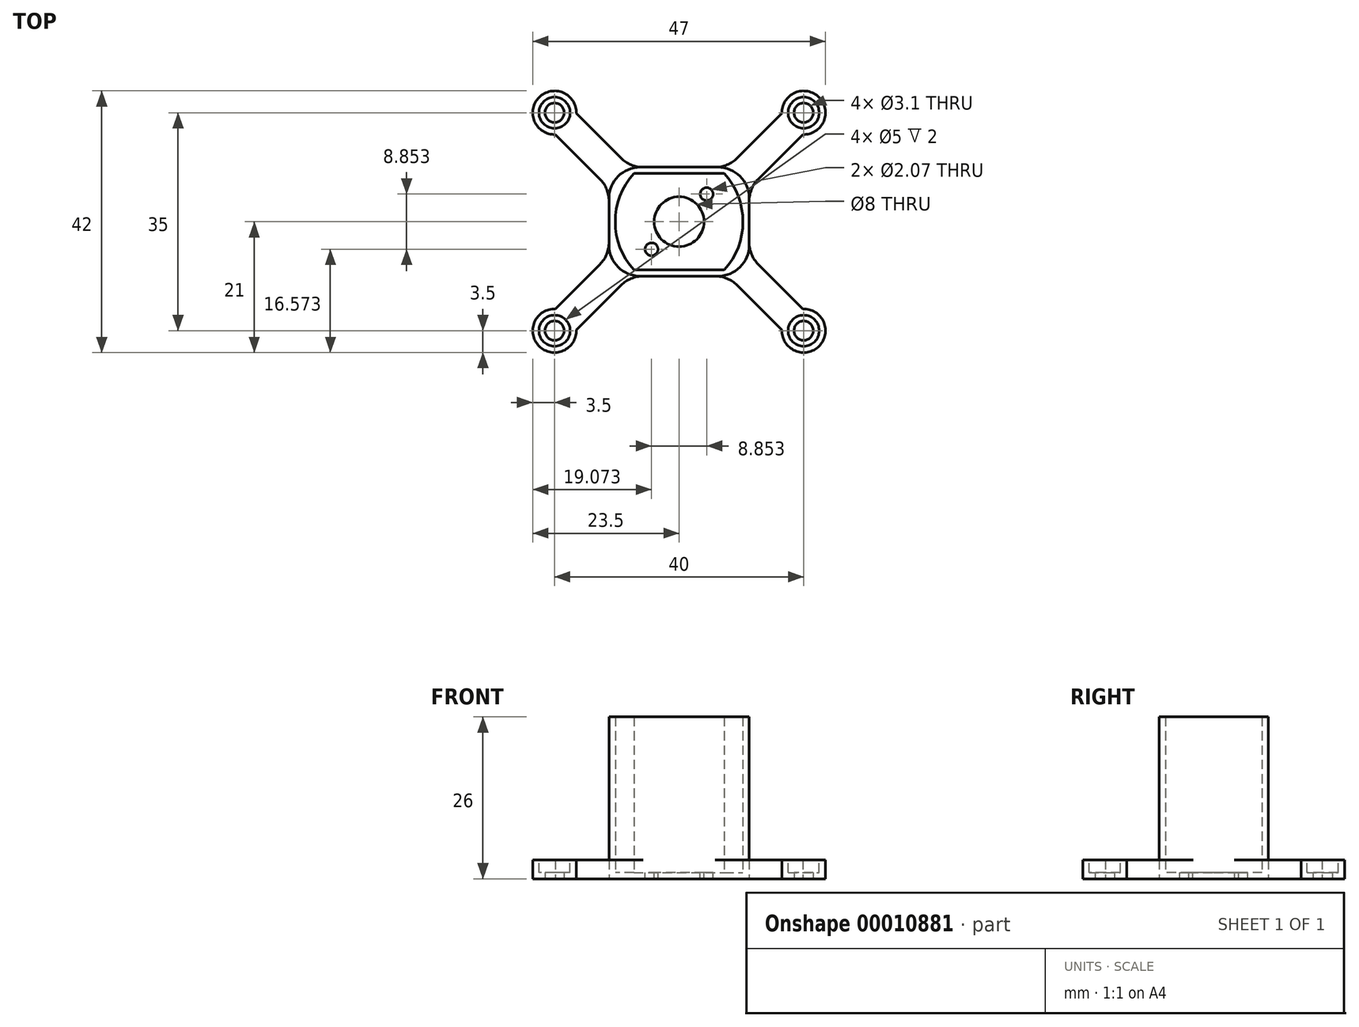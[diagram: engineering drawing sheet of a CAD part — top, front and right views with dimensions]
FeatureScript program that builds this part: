
annotation { "Feature Type Name" : "Feature", "Feature Type Description" : "" }
export const myFeature = defineFeature(function(context is Context, id is Id, definition is map)
    precondition{}
    {
        {
            var Q0;
            Q0=qCreatedBy(makeId("Top.planeOp"),FACE);
            var sketch = newSketch(context, id + "F0", { "sketchPlane" : qUnion([Q0])});
            skLineSegment(sketch, "E0.bottom", {"start": v(-7.25, 7.75) * mm, "end": v(7.25, 7.75) * mm});
            skLineSegment(sketch, "E0.top", {"start": v(-7.25, -7.75) * mm, "end": v(7.25, -7.75) * mm});
            skLineSegment(sketch, "E0.left", {"start": v(-7.25, 7.75) * mm, "end": v(-7.25, -7.75) * mm, "construction": true});
            skLineSegment(sketch, "E0.right", {"start": v(7.25, 7.75) * mm, "end": v(7.25, -7.75) * mm, "construction": true});
            skArc(sketch, "E1", {"start": v(-7.25, 7.75) * mm, "mid": v(-10.25, 0) * mm, "end": v(-7.25, -7.75) * mm});
            skArc(sketch, "E2", {"start": v(7.25, -7.75) * mm, "mid": v(10.25, 0) * mm, "end": v(7.25, 7.75) * mm});
            skLineSegment(sketch, "E3", {"start": v(-7.25, 7.75) * mm, "end": v(-10.25, 7.75) * mm, "construction": true});
            skLineSegment(sketch, "E4", {"start": v(-10.25, 7.75) * mm, "end": v(-10.25, -7.75) * mm, "construction": true});
            skLineSegment(sketch, "E5", {"start": v(-10.25, -7.75) * mm, "end": v(-7.25, -7.75) * mm, "construction": true});
            skLineSegment(sketch, "E6", {"start": v(7.25, -7.75) * mm, "end": v(10.25, -7.75) * mm, "construction": true});
            skLineSegment(sketch, "E7", {"start": v(10.25, -7.75) * mm, "end": v(10.25, 7.75) * mm, "construction": true});
            skLineSegment(sketch, "E8", {"start": v(10.25, 7.75) * mm, "end": v(7.25, 7.75) * mm, "construction": true});
            skLineSegment(sketch, "E9.bottom", {"start": v(-11.25, 8.75) * mm, "end": v(11.25, 8.75) * mm});
            skLineSegment(sketch, "E9.top", {"start": v(-11.25, -8.75) * mm, "end": v(11.25, -8.75) * mm});
            skLineSegment(sketch, "E9.left", {"start": v(-11.25, 8.75) * mm, "end": v(-11.25, -8.75) * mm});
            skLineSegment(sketch, "E9.right", {"start": v(11.25, 8.75) * mm, "end": v(11.25, -8.75) * mm});
            skPoint(sketch, "E10.visualSharp", {"position": v(-11.25, 8.75) * mm});
            skPoint(sketch, "E11.visualSharp", {"position": v(11.25, 8.75) * mm});
            skPoint(sketch, "E12.visualSharp", {"position": v(11.25, -8.75) * mm});
            skPoint(sketch, "E13.visualSharp", {"position": v(-11.25, -8.75) * mm});
            skLineSegment(sketch, "E14", {"start": v(-1.26, 0) * mm, "end": v(1.26, 0) * mm, "construction": true});
            skPoint(sketch, "E15", {"position": v(0, 0) * mm});
            skLineSegment(sketch, "E16", {"start": v(10.25, -7.75) * mm, "end": v(10.25, -8.75) * mm, "construction": true});
            skLineSegment(sketch, "E17", {"start": v(-10.25, 7.75) * mm, "end": v(-10.25, 8.75) * mm, "construction": true});
            skLineSegment(sketch, "E18", {"start": v(-10.25, 7.75) * mm, "end": v(-11.25, 7.75) * mm, "construction": true});
            skLineSegment(sketch, "E19", {"start": v(10.25, -7.75) * mm, "end": v(11.25, -7.75) * mm, "construction": true});
            skSolve(sketch);
        }
        {
            var Q0;
            Q0=qSketchRegion(id+"F0",true);
            extrude(context, id + "F1", {"entities" : qUnion([Q0]), "depth" : 25 * mm});
        }
        {
            var Q0;
            Q0=qCreatedBy(makeId("Top.planeOp"),FACE);
            var sketch = newSketch(context, id + "F2", { "sketchPlane" : qUnion([Q0])});
            skCircle(sketch, "E20", {"center": v(0, 0) * mm, "radius": 4 * mm});
            skLineSegment(sketch, "E21", {"start": v(-4.43, -4.43) * mm, "end": v(4.43, 4.43) * mm, "construction": true});
            skCircle(sketch, "E22", {"center": v(-4.43, -4.43) * mm, "radius": 1.04 * mm});
            skCircle(sketch, "E23", {"center": v(4.43, 4.43) * mm, "radius": 1.04 * mm});
            skLineSegment(sketch, "E24", {"start": v(0, 0) * mm, "end": v(0, -4) * mm, "construction": true});
            skLineSegment(sketch, "E25.bottom", {"start": v(-11.25, -8.75) * mm, "end": v(11.25, -8.75) * mm});
            skLineSegment(sketch, "E25.top", {"start": v(-11.25, 8.75) * mm, "end": v(11.25, 8.75) * mm});
            skLineSegment(sketch, "E25.left", {"start": v(-11.25, -8.75) * mm, "end": v(-11.25, 8.75) * mm});
            skLineSegment(sketch, "E25.right", {"start": v(11.25, -8.75) * mm, "end": v(11.25, 8.75) * mm});
            skSolve(sketch);
        }
        {
            var Q0;
            Q0=qSketchRegion(id+"F2",true);
            extrude(context, id + "F3", {"entities" : qUnion([Q0]), "operationType" : NewBodyOperationType.ADD, "oppositeDirection" : true, "depth" : 1 * mm});
        }
        {
            var Q0;
            Q0=makeQuery(id+"F3.opExtrude","CAP_FACE",FACE,{"disambiguationData":[OSD([sQuery(id+"F2.wireOp",EDGE,"9aef3d48-fcec-49af-8fe0-c07a83de9d9d.bottom"),sQuery(id+"F2.wireOp",EDGE,"9aef3d48-fcec-49af-8fe0-c07a83de9d9d.top"),sQuery(id+"F2.wireOp",EDGE,"9aef3d48-fcec-49af-8fe0-c07a83de9d9d.left"),sQuery(id+"F2.wireOp",EDGE,"9aef3d48-fcec-49af-8fe0-c07a83de9d9d.right"),sQuery(id+"F2.wireOp",EDGE,"60c8d90f-e83d-42f8-a0dd-aa9fc3caf3ca.filletArc"),sQuery(id+"F2.wireOp",EDGE,"e39097f1-45af-4b58-a32d-9713a406a2f0.filletArc"),sQuery(id+"F2.wireOp",EDGE,"80603ea1-f281-4a3c-b745-80a3f8f7ce23.filletArc"),sQuery(id+"F2.wireOp",EDGE,"1a4f9cfa-e126-41bd-9235-e0dfa8cf3aca.filletArc"),sQuery(id+"F2.wireOp",EDGE,"E20"),sQuery(id+"F2.wireOp",EDGE,"E22"),sQuery(id+"F2.wireOp",EDGE,"E23")])],"isStart":false});
            var sketch = newSketch(context, id + "F4", { "sketchPlane" : qUnion([Q0])});
            skCircle(sketch, "E26", {"center": v(0, 0) * mm, "radius": 17.67 * mm, "construction": true});
            skLineSegment(sketch, "E27", {"start": v(-9.34, 10.21) * mm, "end": v(-16.5, 17.38) * mm});
            skLineSegment(sketch, "E28", {"start": v(-12.71, 6.84) * mm, "end": v(-19.88, 14) * mm});
            skLineSegment(sketch, "E29", {"start": v(-11.25, 8.75) * mm, "end": v(-20, 17.5) * mm, "construction": true});
            skCircle(sketch, "E30", {"center": v(-20, 17.5) * mm, "radius": 1.55 * mm});
            skLineSegment(sketch, "E31", {"start": v(-7.87, 8.75) * mm, "end": v(-11.25, 8.75) * mm, "construction": true});
            skLineSegment(sketch, "E32", {"start": v(-11.25, 8.75) * mm, "end": v(-11.25, 5.37) * mm, "construction": true});
            skPoint(sketch, "E33.visualSharp", {"position": v(-7.87, 8.75) * mm});
            skArc(sketch, "E33.filletArc", {"start": v(-9.34, 10.21) * mm, "mid": v(-7.71, 9.13) * mm, "end": v(-5.8, 8.75) * mm});
            skPoint(sketch, "E34.visualSharp", {"position": v(-11.25, 5.37) * mm});
            skArc(sketch, "E34.filletArc", {"start": v(-11.25, 3.3) * mm, "mid": v(-11.63, 5.21) * mm, "end": v(-12.71, 6.84) * mm});
            skLineSegment(sketch, "E35", {"start": v(-11.25, 3.3) * mm, "end": v(-11.25, 8.75) * mm});
            skLineSegment(sketch, "E36", {"start": v(-5.8, 8.75) * mm, "end": v(-11.25, 8.75) * mm});
            skArc(sketch, "E37", {"start": v(-16.5, 17.38) * mm, "mid": v(-22.47, 19.97) * mm, "end": v(-19.88, 14) * mm});
            skSolve(sketch);
        }
        {
            var Q0;
            Q0=qSketchRegion(id+"F4",true);
            extrude(context, id + "F5", {"entities" : qUnion([Q0]), "oppositeDirection" : true, "depth" : 3 * mm});
        }
        {
            var Q0;
            Q0=makeQuery(id+"F5.opExtrude","CAP_FACE",FACE,{"disambiguationData":[OSD([sQuery(id+"F4.wireOp",EDGE,"E27"),sQuery(id+"F4.wireOp",EDGE,"E28"),sQuery(id+"F4.wireOp",EDGE,"E30"),sQuery(id+"F4.wireOp",EDGE,"E33.filletArc"),sQuery(id+"F4.wireOp",EDGE,"E34.filletArc"),sQuery(id+"F4.wireOp",EDGE,"E35"),sQuery(id+"F4.wireOp",EDGE,"E36"),sQuery(id+"F4.wireOp",EDGE,"E37")])],"isStart":false});
            var sketch = newSketch(context, id + "F6", { "sketchPlane" : qUnion([Q0])});
            skCircle(sketch, "E38", {"center": v(-20, -17.5) * mm, "radius": 2.5 * mm});
            skSolve(sketch);
        }
        {
            var Q0;
            Q0 = qSketchRegion(id + "F6", true);
            extrude(context, id + "F7", {"entities" : qUnion([Q0]), "operationType" : NewBodyOperationType.REMOVE, "oppositeDirection" : true, "depth" : 2 * mm});
        }
        {
            var Q0;
            Q0=makeQuery(id+"F5.opExtrude","SWEPT_BODY",BODY,{"disambiguationData":[OSD([sQuery(id+"F4.wireOp",EDGE,"E27"),sQuery(id+"F4.wireOp",EDGE,"E28"),sQuery(id+"F4.wireOp",EDGE,"1cbfcee3-eb8b-4ad0-8d0a-d4f1d73b6d58"),sQuery(id+"F4.wireOp",EDGE,"E30"),sQuery(id+"F4.wireOp",EDGE,"E33.filletArc"),sQuery(id+"F4.wireOp",EDGE,"E34.filletArc"),sQuery(id+"F4.wireOp",EDGE,"E35"),sQuery(id+"F4.wireOp",EDGE,"E36")])]});
            var Q1;
            Q1=qCreatedBy(makeId("Front.planeOp"),FACE);
            mirror(context, id + "F8", {"entities" : qUnion([Q0]), "mirrorPlane" : qUnion([Q1])});
        }
        {
            var Q0;
            Q0=makeQuery(id+"F8.opPattern","COPY",BODY,{"derivedFrom":makeQuery(id+"F5.opExtrude","SWEPT_BODY",BODY,{"disambiguationData":[OSD([sQuery(id+"F4.wireOp",EDGE,"E27"),sQuery(id+"F4.wireOp",EDGE,"E28"),sQuery(id+"F4.wireOp",EDGE,"1cbfcee3-eb8b-4ad0-8d0a-d4f1d73b6d58"),sQuery(id+"F4.wireOp",EDGE,"E30"),sQuery(id+"F4.wireOp",EDGE,"E33.filletArc"),sQuery(id+"F4.wireOp",EDGE,"E34.filletArc"),sQuery(id+"F4.wireOp",EDGE,"E35"),sQuery(id+"F4.wireOp",EDGE,"E36")])]}),"instanceName":"1"});
            var Q1;
            Q1=makeQuery(id+"F5.opExtrude","SWEPT_BODY",BODY,{"disambiguationData":[OSD([sQuery(id+"F4.wireOp",EDGE,"E27"),sQuery(id+"F4.wireOp",EDGE,"E28"),sQuery(id+"F4.wireOp",EDGE,"1cbfcee3-eb8b-4ad0-8d0a-d4f1d73b6d58"),sQuery(id+"F4.wireOp",EDGE,"E30"),sQuery(id+"F4.wireOp",EDGE,"E33.filletArc"),sQuery(id+"F4.wireOp",EDGE,"E34.filletArc"),sQuery(id+"F4.wireOp",EDGE,"E35"),sQuery(id+"F4.wireOp",EDGE,"E36")])]});
            var Q2;
            Q2=qCreatedBy(makeId("Right.planeOp"),FACE);
            mirror(context, id + "F9", {"operationType" : NewBodyOperationType.ADD, "entities" : qUnion([Q0, Q1]), "mirrorPlane" : qUnion([Q2])});
        }
        {
            var Q0;
            Q0=makeQuery(id+"F3.boolean.opBoolean","MERGE",EDGE,{"derivedFrom":[makeQuery(id+"F1.opExtrude","SWEPT_EDGE",EDGE,{"disambiguationData":[OSD([sQuery(id+"F0.wireOp",EDGE,"E9.bottom"),sQuery(id+"F0.wireOp",EDGE,"E9.left")])]}),makeQuery(id+"F3.opExtrude","SWEPT_EDGE",EDGE,{"disambiguationData":[OSD([sQuery(id+"F2.wireOp",EDGE,"E25.top"),sQuery(id+"F2.wireOp",EDGE,"E25.left")])]})]});
            var Q1;
            Q1=makeQuery(id+"F3.boolean.opBoolean","MERGE",EDGE,{"derivedFrom":[makeQuery(id+"F1.opExtrude","SWEPT_EDGE",EDGE,{"disambiguationData":[OSD([sQuery(id+"F0.wireOp",EDGE,"E9.top"),sQuery(id+"F0.wireOp",EDGE,"E9.left")])]}),makeQuery(id+"F3.opExtrude","SWEPT_EDGE",EDGE,{"disambiguationData":[OSD([sQuery(id+"F2.wireOp",EDGE,"E25.bottom"),sQuery(id+"F2.wireOp",EDGE,"E25.left")])]})]});
            var Q2;
            Q2=makeQuery(id+"F3.boolean.opBoolean","MERGE",EDGE,{"derivedFrom":[makeQuery(id+"F1.opExtrude","SWEPT_EDGE",EDGE,{"disambiguationData":[OSD([sQuery(id+"F0.wireOp",EDGE,"E9.top"),sQuery(id+"F0.wireOp",EDGE,"E9.right")])]}),makeQuery(id+"F3.opExtrude","SWEPT_EDGE",EDGE,{"disambiguationData":[OSD([sQuery(id+"F2.wireOp",EDGE,"E25.bottom"),sQuery(id+"F2.wireOp",EDGE,"E25.right")])]})]});
            var Q3;
            Q3=makeQuery(id+"F3.boolean.opBoolean","MERGE",EDGE,{"derivedFrom":[makeQuery(id+"F1.opExtrude","SWEPT_EDGE",EDGE,{"disambiguationData":[OSD([sQuery(id+"F0.wireOp",EDGE,"E9.bottom"),sQuery(id+"F0.wireOp",EDGE,"E9.right")])]}),makeQuery(id+"F3.opExtrude","SWEPT_EDGE",EDGE,{"disambiguationData":[OSD([sQuery(id+"F2.wireOp",EDGE,"E25.top"),sQuery(id+"F2.wireOp",EDGE,"E25.right")])]})]});
            fillet(context, id + "F10", {"entities" : qUnion([Q0, Q1, Q2, Q3]), "radius" : 5 * mm, "tangentPropagation" : true, "allowEdgeOverflow" : false});
        }
    });
